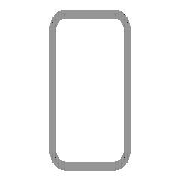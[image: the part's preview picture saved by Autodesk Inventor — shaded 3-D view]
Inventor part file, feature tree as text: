
AUTODESK INVENTOR PART (.ipt)
format: ipt  version: 2025.1 (Build 291241020, 241B)  size: 142,848 bytes
history: native  units: mm (DEFAULTED — no unit token found)
features: other x4, plane x2, split x1, sketch x1
ambient origin geometry x8: Origin, YZ Plane, XZ Plane, XY Plane, X Axis, Y Axis, Z Axis, Center Point
bodies: Solid1 (feature_tree), Body (feature_tree)
feature tree (8):
  parser-record x1  (decoder bookkeeping rows leaked as tree rows — omitted from the tree; the rows remain in map.json)
  other  "Driven Length"
  other  "Start Plane"
  other  "End Plane"
  plane  "Work Plane4"
  split  "Split1"
  sketch  "Sketch3"  dims[d3=863.237711mm d4=0.0mm d7=4.0mm d9=20.0mm d11=40.0mm d12=2.0mm d13=-0.0mm d14=863.237711mm d15=10.0mm d16=20.0mm d17=90.0deg d18=863.237711mm]
  plane  "Work Plane3"
